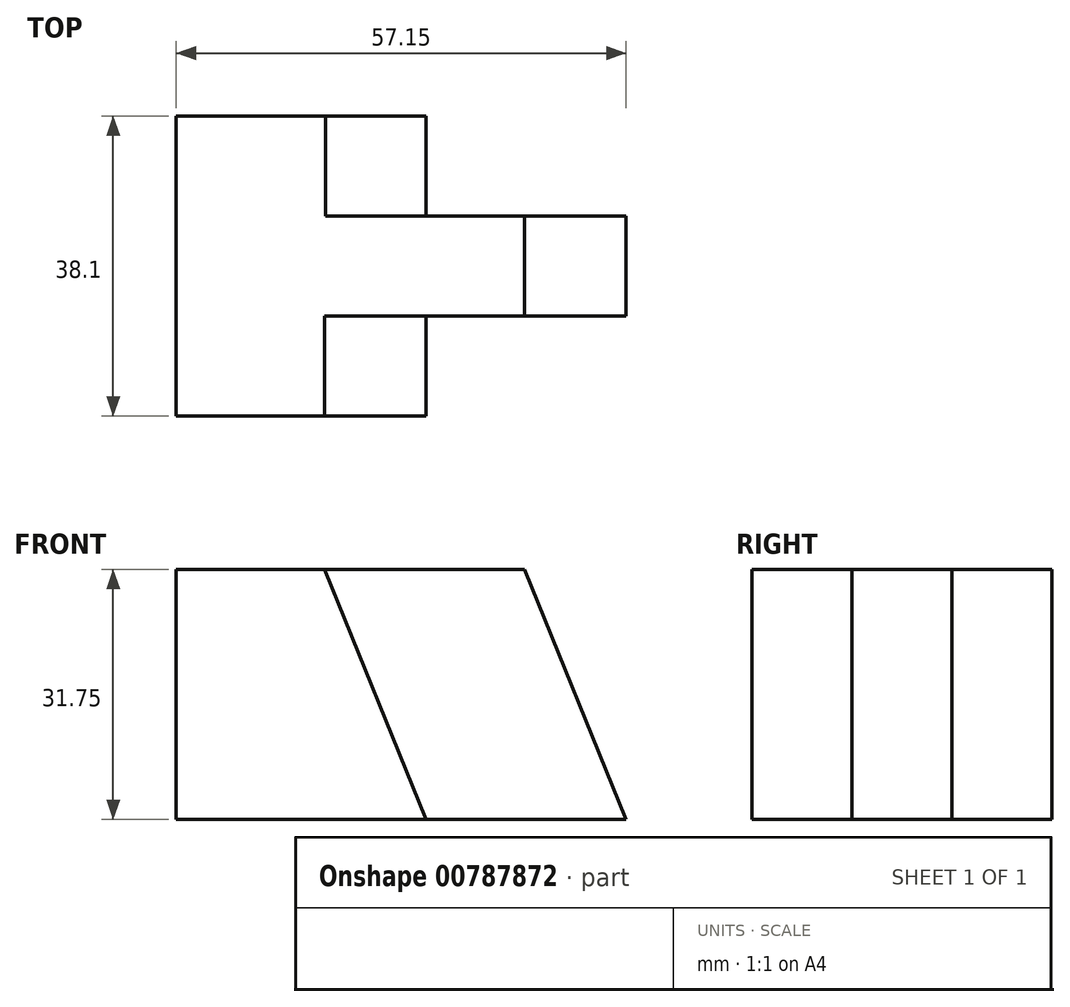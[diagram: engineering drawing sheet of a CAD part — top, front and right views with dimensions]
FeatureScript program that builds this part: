
annotation { "Feature Type Name" : "Feature", "Feature Type Description" : "" }
export const myFeature = defineFeature(function(context is Context, id is Id, definition is map)
    precondition{}
    {
        {
            var Q0;
            Q0=qCreatedBy(makeId("Front.planeOp"),FACE);
            var sketch = newSketch(context, id + "F0", { "sketchPlane" : qUnion([Q0])});
            skLineSegment(sketch, "E0", {"start": v(0, 0) * mm, "end": v(57.15, 0) * mm});
            skLineSegment(sketch, "E1", {"start": v(57.15, 0) * mm, "end": v(57.15, 31.75) * mm});
            skLineSegment(sketch, "E2", {"start": v(57.15, 31.75) * mm, "end": v(0, 31.75) * mm});
            skLineSegment(sketch, "E3", {"start": v(0, 31.75) * mm, "end": v(0, 0) * mm});
            skSolve(sketch);
        }
        {
            var Q0;
            Q0 = qSketchRegion(id + "F0", true);
            extrude(context, id + "F1", {"entities" : qUnion([Q0]), "depth" : 38.1 * mm, "offsetDistance" : 25.4 * mm});
        }
        {
            var Q0;
            Q0=makeQuery(id+"F1.opExtrude","CAP_FACE",FACE,{"disambiguationData":[OSD([sQuery(id+"F0.wireOp",EDGE,"E0"),sQuery(id+"F0.wireOp",EDGE,"E1"),sQuery(id+"F0.wireOp",EDGE,"E2"),sQuery(id+"F0.wireOp",EDGE,"E3")])],"isStart":false});
            var sketch = newSketch(context, id + "F2", { "sketchPlane" : qUnion([Q0])});
            skLineSegment(sketch, "E4", {"start": v(0, 0) * mm, "end": v(31.75, 0) * mm});
            skLineSegment(sketch, "E5", {"start": v(31.75, 0) * mm, "end": v(18.84, 31.75) * mm});
            skLineSegment(sketch, "E6", {"start": v(18.84, 31.75) * mm, "end": v(31.75, 31.75) * mm});
            skLineSegment(sketch, "E7", {"start": v(31.75, 31.75) * mm, "end": v(18.84, 31.75) * mm});
            skLineSegment(sketch, "E8", {"start": v(31.75, 31.75) * mm, "end": v(31.75, 0) * mm});
            skLineSegment(sketch, "E9", {"start": v(31.75, 0) * mm, "end": v(57.15, 0) * mm});
            skLineSegment(sketch, "E10", {"start": v(57.15, 0) * mm, "end": v(57.15, 31.75) * mm});
            skLineSegment(sketch, "E11", {"start": v(57.15, 31.75) * mm, "end": v(31.75, 31.75) * mm});
            skSolve(sketch);
        }
        {
            var Q0;
            Q0=makeQuery(id+"F2.imprint","IMPRINT",FACE,{"disambiguationData":[TD([[makeQuery(id+"F2.imprint","IMPRINT",EDGE,{"derivedFrom":sQuery(id+"F2.wireOp",EDGE,"E8")}),1.0]])]});
            extrude(context, id + "F3", {"entities" : qUnion([Q0]), "operationType" : NewBodyOperationType.REMOVE, "oppositeDirection" : true, "depth" : 12.7 * mm, "offsetDistance" : 25.4 * mm});
        }
        {
            var Q0;
            Q0=makeQuery(id+"F2.imprint","IMPRINT",FACE,{"disambiguationData":[TD([[makeQuery(id+"F2.imprint","IMPRINT",EDGE,{"derivedFrom":sQuery(id+"F2.wireOp",EDGE,"E5")}),-1.0]])]});
            extrude(context, id + "F4", {"entities" : qUnion([Q0]), "operationType" : NewBodyOperationType.REMOVE, "oppositeDirection" : true, "depth" : 12.7 * mm, "offsetDistance" : 25.4 * mm});
        }
        {
            var Q0;
            {var subQ0=sQuery(id+"F2.wireOp",EDGE,"E8");Q0=makeQuery(id+"F4.boolean.opBoolean","MERGE",FACE,{"derivedFrom":[makeQuery(id+"F3.boolean.opBoolean","COPY",FACE,{"derivedFrom":makeQuery(id+"F3.opExtrude","CAP_FACE",FACE,{"disambiguationData":[OSD([subQ0,sQuery(id+"F2.wireOp",EDGE,"E9"),sQuery(id+"F2.wireOp",EDGE,"E10"),sQuery(id+"F2.wireOp",EDGE,"E11")])],"isStart":false})}),makeQuery(id+"F4.opExtrude","CAP_FACE",FACE,{"disambiguationData":[OSD([sQuery(id+"F2.wireOp",EDGE,"E5"),sQuery(id+"F2.wireOp",EDGE,"E7"),subQ0])],"isStart":false})]});}
            var sketch = newSketch(context, id + "F5", { "sketchPlane" : qUnion([Q0])});
            skLineSegment(sketch, "E12", {"start": v(31.75, 0) * mm, "end": v(57.15, 0) * mm});
            skLineSegment(sketch, "E13", {"start": v(57.15, 0) * mm, "end": v(18.84, 31.75) * mm});
            skLineSegment(sketch, "E14", {"start": v(18.84, 31.75) * mm, "end": v(44.24, 31.75) * mm});
            skLineSegment(sketch, "E15", {"start": v(44.24, 31.75) * mm, "end": v(57.15, 0) * mm});
            skLineSegment(sketch, "E16", {"start": v(57.15, 31.75) * mm, "end": v(44.24, 31.75) * mm});
            skSolve(sketch);
        }
        {
            var Q0;
            Q0=makeQuery(id+"F5.imprint","IMPRINT",FACE,{"disambiguationData":[TD([[makeQuery(id+"F5.imprint","IMPRINT",EDGE,{"derivedFrom":sQuery(id+"F5.wireOp",EDGE,"E15")}),1.0]])]});
            extrude(context, id + "F6", {"entities" : qUnion([Q0]), "operationType" : NewBodyOperationType.REMOVE, "oppositeDirection" : true, "depth" : 12.7 * mm, "offsetDistance" : 25.4 * mm});
        }
        {
            var Q0;
            Q0=makeQuery(id+"F1.opExtrude","CAP_FACE",FACE,{"disambiguationData":[OSD([sQuery(id+"F0.wireOp",EDGE,"E0"),sQuery(id+"F0.wireOp",EDGE,"E1"),sQuery(id+"F0.wireOp",EDGE,"E2"),sQuery(id+"F0.wireOp",EDGE,"E3")])],"isStart":true});
            var sketch = newSketch(context, id + "F7", { "sketchPlane" : qUnion([Q0])});
            skLineSegment(sketch, "E17", {"start": v(0, 0) * mm, "end": v(-31.75, 0) * mm});
            skLineSegment(sketch, "E18", {"start": v(-31.75, 0) * mm, "end": v(-18.98, 31.75) * mm});
            skSolve(sketch);
        }
        {
            var Q0;
            {var subQ0=sQuery(id+"F7.wireOp",EDGE,"E18");Q0=makeQuery(id+"F7.imprint","IMPRINT",FACE,{"disambiguationData":[TD([[makeQuery(id+"F7.imprint","IMPRINT",EDGE,{"derivedFrom":subQ0}),1.0]])]});}
            extrude(context, id + "F8", {"entities" : qUnion([Q0]), "operationType" : NewBodyOperationType.REMOVE, "oppositeDirection" : true, "depth" : 12.7 * mm, "offsetDistance" : 25.4 * mm});
        }
    });
